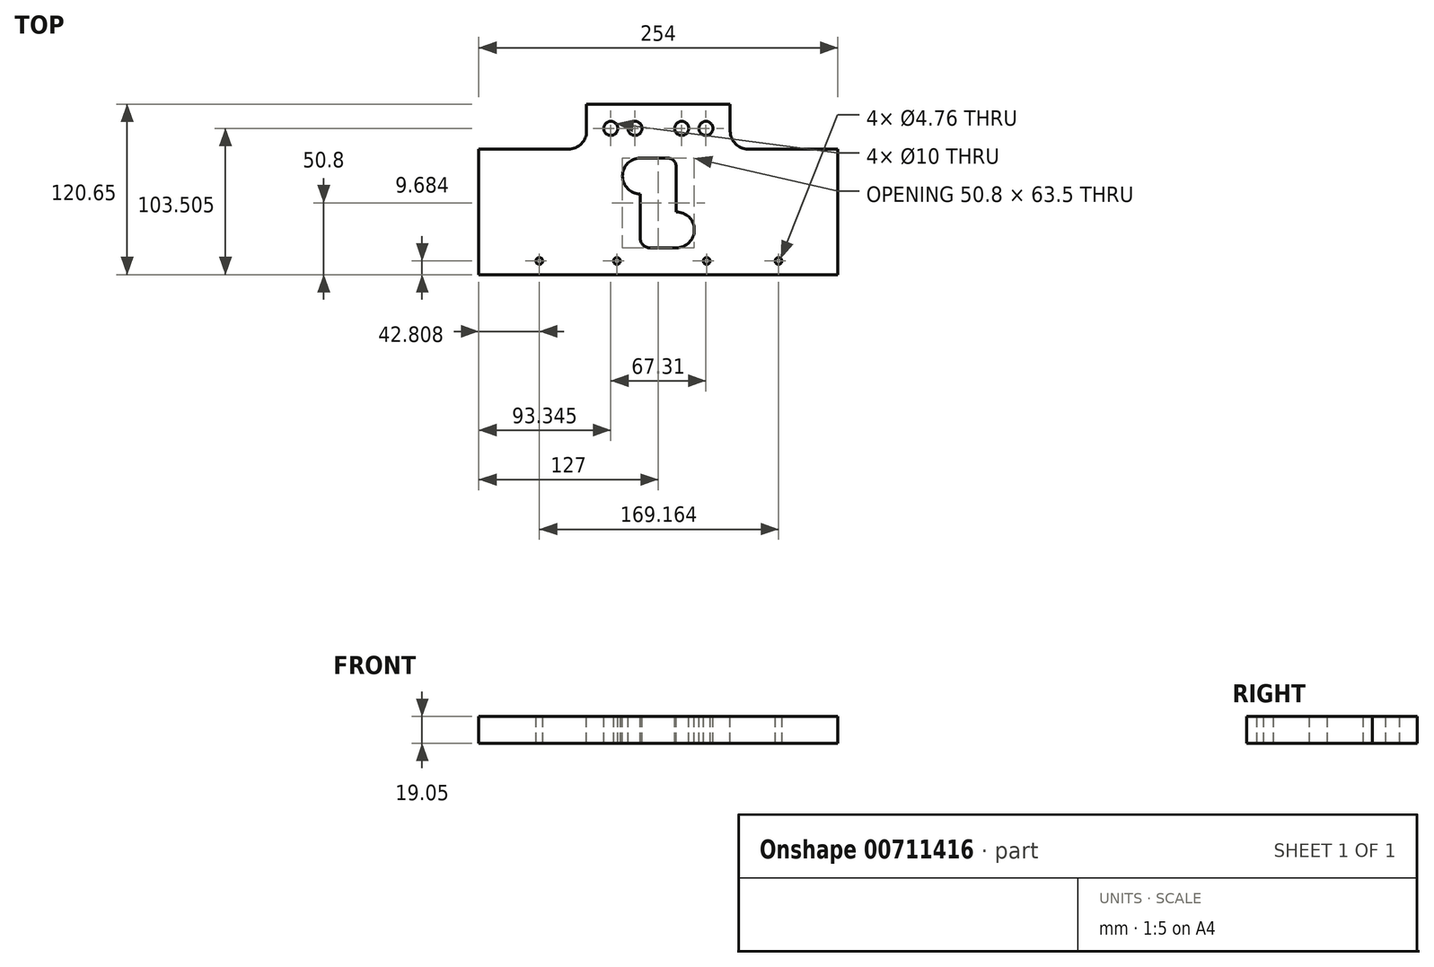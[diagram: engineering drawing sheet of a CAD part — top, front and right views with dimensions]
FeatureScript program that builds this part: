
annotation { "Feature Type Name" : "Feature", "Feature Type Description" : "" }
export const myFeature = defineFeature(function(context is Context, id is Id, definition is map)
    precondition{}
    {
        {
            var Q0;
            Q0=qCreatedBy(makeId("Top.planeOp"),FACE);
            var sketch = newSketch(context, id + "F0", { "sketchPlane" : qUnion([Q0])});
            skLineSegment(sketch, "E0.bottom", {"start": v(12.7, -31.75) * mm, "end": v(-6.35, -31.75) * mm});
            skLineSegment(sketch, "E0.top", {"start": v(6.35, 31.75) * mm, "end": v(-12.7, 31.75) * mm});
            skLineSegment(sketch, "E0.right", {"start": v(-12.7, -25.4) * mm, "end": v(-12.7, 6.35) * mm});
            skPoint(sketch, "E0.middle", {"position": v(0, 0) * mm});
            skArc(sketch, "E1", {"start": v(-12.7, 31.75) * mm, "mid": v(-25.4, 19.05) * mm, "end": v(-12.7, 6.35) * mm});
            skArc(sketch, "E2", {"start": v(12.7, -31.75) * mm, "mid": v(25.4, -19.05) * mm, "end": v(12.7, -6.35) * mm});
            skLineSegment(sketch, "E3.trimOffspring", {"start": v(12.7, -6.35) * mm, "end": v(12.7, 25.4) * mm});
            skPoint(sketch, "E4.visualSharp", {"position": v(-12.7, -31.75) * mm});
            skArc(sketch, "E4.filletArc", {"start": v(-12.7, -25.4) * mm, "mid": v(-10.84, -29.9) * mm, "end": v(-6.35, -31.75) * mm});
            skPoint(sketch, "E5.visualSharp", {"position": v(12.7, 31.75) * mm});
            skArc(sketch, "E5.filletArc", {"start": v(12.7, 25.4) * mm, "mid": v(10.84, 29.9) * mm, "end": v(6.35, 31.75) * mm});
            skLineSegment(sketch, "E6.bottom", {"start": v(0, -19.05) * mm, "end": v(-6.35, -19.05) * mm});
            skLineSegment(sketch, "E6.top", {"start": v(0, 19.05) * mm, "end": v(-6.35, 19.05) * mm});
            skLineSegment(sketch, "E6.left", {"start": v(6.35, -12.7) * mm, "end": v(6.35, 12.7) * mm});
            skLineSegment(sketch, "E6.right", {"start": v(-6.35, -19.05) * mm, "end": v(-6.35, 19.05) * mm});
            skPoint(sketch, "E7.visualSharp", {"position": v(6.35, 19.05) * mm});
            skArc(sketch, "E7.filletArc", {"start": v(6.35, 12.7) * mm, "mid": v(4.5, 17.2) * mm, "end": v(0, 19.05) * mm});
            skPoint(sketch, "E8.visualSharp", {"position": v(6.35, -19.05) * mm});
            skArc(sketch, "E8.filletArc", {"start": v(0, -19.05) * mm, "mid": v(4.5, -17.2) * mm, "end": v(6.35, -12.7) * mm});
            skLineSegment(sketch, "E9.top", {"start": v(50.8, -50.8) * mm, "end": v(-50.8, -50.8) * mm});
            skLineSegment(sketch, "E10.top", {"start": v(-50.8, 69.85) * mm, "end": v(50.8, 69.85) * mm});
            skLineSegment(sketch, "E11", {"start": v(50.8, -50.8) * mm, "end": v(50.8, -50.8) * mm});
            skLineSegment(sketch, "E12", {"start": v(-50.8, -50.8) * mm, "end": v(-50.8, -50.8) * mm});
            skCircle(sketch, "E13", {"center": v(-33.66, 52.7) * mm, "radius": 5 * mm});
            skCircle(sketch, "E14", {"center": v(-16.51, 52.7) * mm, "radius": 5 * mm});
            skCircle(sketch, "E15", {"center": v(16.5, 52.7) * mm, "radius": 5 * mm});
            skCircle(sketch, "E16", {"center": v(33.65, 52.7) * mm, "radius": 5 * mm});
            skLineSegment(sketch, "E17.top", {"start": v(127, 38.1) * mm, "end": v(63.5, 38.1) * mm});
            skLineSegment(sketch, "E17.left", {"start": v(127, -38.1) * mm, "end": v(127, 38.1) * mm});
            skLineSegment(sketch, "E17.right", {"start": v(-127, -38.1) * mm, "end": v(-127, 38.1) * mm});
            skLineSegment(sketch, "E18.trimOffspring", {"start": v(-63.5, 38.1) * mm, "end": v(-127, 38.1) * mm});
            skLineSegment(sketch, "E19", {"start": v(-50.8, 69.85) * mm, "end": v(-50.8, 50.8) * mm});
            skLineSegment(sketch, "E20", {"start": v(50.8, 69.85) * mm, "end": v(50.8, 50.8) * mm});
            skPoint(sketch, "E21.visualSharp", {"position": v(-50.8, 38.1) * mm});
            skArc(sketch, "E21.filletArc", {"start": v(-63.5, 38.1) * mm, "mid": v(-54.52, 41.82) * mm, "end": v(-50.8, 50.8) * mm});
            skPoint(sketch, "E22.visualSharp", {"position": v(50.8, 38.1) * mm});
            skArc(sketch, "E22.filletArc", {"start": v(50.8, 50.8) * mm, "mid": v(54.52, 41.82) * mm, "end": v(63.5, 38.1) * mm});
            skLineSegment(sketch, "E23.top", {"start": v(-127, -50.8) * mm, "end": v(-50.8, -50.8) * mm});
            skLineSegment(sketch, "E23.left", {"start": v(-127, -38.1) * mm, "end": v(-127, -50.8) * mm});
            skLineSegment(sketch, "E24.bottom", {"start": v(50.8, -50.8) * mm, "end": v(127, -50.8) * mm});
            skLineSegment(sketch, "E24.right", {"start": v(127, -50.8) * mm, "end": v(127, -38.1) * mm});
            skLineSegment(sketch, "E25", {"start": v(-45.75, 37.46) * mm, "end": v(40.3, 37.46) * mm, "construction": true});
            skLineSegment(sketch, "E26", {"start": v(-126.28, -38.74) * mm, "end": v(126.43, -38.74) * mm, "construction": true});
            skCircle(sketch, "E27", {"center": v(34.17, -41.12) * mm, "radius": 2.38 * mm});
            skLineSegment(sketch, "E28", {"start": v(34.17, -41.12) * mm, "end": v(124.12, -41.12) * mm});
            skLineSegment(sketch, "E29", {"start": v(34.17, -41.12) * mm, "end": v(-125.44, -41.12) * mm});
            skCircle(sketch, "E30", {"center": v(-29.33, -41.12) * mm, "radius": 2.38 * mm});
            skCircle(sketch, "E31.1.0.0", {"center": v(-84.2, -41.12) * mm, "radius": 2.38 * mm});
            skCircle(sketch, "E32.2.0.0", {"center": v(84.97, -41.12) * mm, "radius": 2.38 * mm});
            skLineSegment(sketch, "E32.direction1", {"start": v(34.17, -41.12) * mm, "end": v(59.57, -41.12) * mm, "construction": true});
            skSolve(sketch);
        }
        {
            var Q0;
            Q0 = qSketchRegion(id + "F0", true);
            extrude(context, id + "F1", {"entities" : qUnion([Q0]), "depth" : -19.05 * mm, "offsetDistance" : 25.4 * mm});
        }
        {
            var Q0;
            Q0=makeQuery(id+"F1.opExtrude","SWEPT_BODY",BODY,{"disambiguationData":[OSD([sQuery(id+"F0.wireOp",EDGE,"E0.bottom"),sQuery(id+"F0.wireOp",EDGE,"E0.top"),sQuery(id+"F0.wireOp",EDGE,"E0.right"),sQuery(id+"F0.wireOp",EDGE,"E1"),sQuery(id+"F0.wireOp",EDGE,"E2"),sQuery(id+"F0.wireOp",EDGE,"E3.trimOffspring"),sQuery(id+"F0.wireOp",EDGE,"E4.filletArc"),sQuery(id+"F0.wireOp",EDGE,"E5.filletArc"),sQuery(id+"F0.wireOp",EDGE,"E9.top"),sQuery(id+"F0.wireOp",EDGE,"E10.top"),sQuery(id+"F0.wireOp",EDGE,"E13"),sQuery(id+"F0.wireOp",EDGE,"E14"),sQuery(id+"F0.wireOp",EDGE,"E15"),sQuery(id+"F0.wireOp",EDGE,"E16"),sQuery(id+"F0.wireOp",EDGE,"E17.top"),sQuery(id+"F0.wireOp",EDGE,"E17.left"),sQuery(id+"F0.wireOp",EDGE,"E17.right"),sQuery(id+"F0.wireOp",EDGE,"E18.trimOffspring"),sQuery(id+"F0.wireOp",EDGE,"E19"),sQuery(id+"F0.wireOp",EDGE,"E20"),sQuery(id+"F0.wireOp",EDGE,"E21.filletArc"),sQuery(id+"F0.wireOp",EDGE,"E22.filletArc"),sQuery(id+"F0.wireOp",EDGE,"E23.top"),sQuery(id+"F0.wireOp",EDGE,"E23.left"),sQuery(id+"F0.wireOp",EDGE,"E24.bottom"),sQuery(id+"F0.wireOp",EDGE,"E24.right"),sQuery(id+"F0.wireOp",EDGE,"E27"),sQuery(id+"F0.wireOp",EDGE,"E30"),sQuery(id+"F0.wireOp",EDGE,"E31.1.0.0"),sQuery(id+"F0.wireOp",EDGE,"E32.2.0.0")])]});
            transform(context, id + "F2", {"entities" : qUnion([Q0]), "transformType" : TransformType.TRANSLATION_3D, "dx" : 0 * mm, "dy" : 0 * mm, "dz" : 0 * mm, "makeCopy" : true});
        }
        {
            var Q0;
            Q0=makeQuery(id+"F2.opPattern","COPY",BODY,{"derivedFrom":makeQuery(id+"F1.opExtrude","SWEPT_BODY",BODY,{"disambiguationData":[OSD([sQuery(id+"F0.wireOp",EDGE,"E0.bottom"),sQuery(id+"F0.wireOp",EDGE,"E0.top"),sQuery(id+"F0.wireOp",EDGE,"E0.right"),sQuery(id+"F0.wireOp",EDGE,"E1"),sQuery(id+"F0.wireOp",EDGE,"E2"),sQuery(id+"F0.wireOp",EDGE,"E3.trimOffspring"),sQuery(id+"F0.wireOp",EDGE,"E4.filletArc"),sQuery(id+"F0.wireOp",EDGE,"E5.filletArc"),sQuery(id+"F0.wireOp",EDGE,"E9.top"),sQuery(id+"F0.wireOp",EDGE,"E10.top"),sQuery(id+"F0.wireOp",EDGE,"E13"),sQuery(id+"F0.wireOp",EDGE,"E14"),sQuery(id+"F0.wireOp",EDGE,"E15"),sQuery(id+"F0.wireOp",EDGE,"E16"),sQuery(id+"F0.wireOp",EDGE,"E17.top"),sQuery(id+"F0.wireOp",EDGE,"E17.left"),sQuery(id+"F0.wireOp",EDGE,"E17.right"),sQuery(id+"F0.wireOp",EDGE,"E18.trimOffspring"),sQuery(id+"F0.wireOp",EDGE,"E19"),sQuery(id+"F0.wireOp",EDGE,"E20"),sQuery(id+"F0.wireOp",EDGE,"E21.filletArc"),sQuery(id+"F0.wireOp",EDGE,"E22.filletArc"),sQuery(id+"F0.wireOp",EDGE,"E23.top"),sQuery(id+"F0.wireOp",EDGE,"E23.left"),sQuery(id+"F0.wireOp",EDGE,"E24.bottom"),sQuery(id+"F0.wireOp",EDGE,"E24.right"),sQuery(id+"F0.wireOp",EDGE,"E27"),sQuery(id+"F0.wireOp",EDGE,"E30"),sQuery(id+"F0.wireOp",EDGE,"E31.1.0.0"),sQuery(id+"F0.wireOp",EDGE,"E32.2.0.0")])]}),"instanceName":"1"});
            deleteBodies(context, id + "F3", {"entities" : qUnion([Q0])});
        }
        {
            var Q0;
            Q0=makeQuery(id+"F1.opExtrude","SWEPT_BODY",BODY,{"disambiguationData":[OSD([sQuery(id+"F0.wireOp",EDGE,"E0.bottom"),sQuery(id+"F0.wireOp",EDGE,"E0.top"),sQuery(id+"F0.wireOp",EDGE,"E0.right"),sQuery(id+"F0.wireOp",EDGE,"E1"),sQuery(id+"F0.wireOp",EDGE,"E2"),sQuery(id+"F0.wireOp",EDGE,"E3.trimOffspring"),sQuery(id+"F0.wireOp",EDGE,"E4.filletArc"),sQuery(id+"F0.wireOp",EDGE,"E5.filletArc"),sQuery(id+"F0.wireOp",EDGE,"E9.top"),sQuery(id+"F0.wireOp",EDGE,"E10.top"),sQuery(id+"F0.wireOp",EDGE,"E13"),sQuery(id+"F0.wireOp",EDGE,"E14"),sQuery(id+"F0.wireOp",EDGE,"E15"),sQuery(id+"F0.wireOp",EDGE,"E16"),sQuery(id+"F0.wireOp",EDGE,"E17.top"),sQuery(id+"F0.wireOp",EDGE,"E17.left"),sQuery(id+"F0.wireOp",EDGE,"E17.right"),sQuery(id+"F0.wireOp",EDGE,"E18.trimOffspring"),sQuery(id+"F0.wireOp",EDGE,"E19"),sQuery(id+"F0.wireOp",EDGE,"E20"),sQuery(id+"F0.wireOp",EDGE,"E21.filletArc"),sQuery(id+"F0.wireOp",EDGE,"E22.filletArc"),sQuery(id+"F0.wireOp",EDGE,"E23.top"),sQuery(id+"F0.wireOp",EDGE,"E23.left"),sQuery(id+"F0.wireOp",EDGE,"E24.bottom"),sQuery(id+"F0.wireOp",EDGE,"E24.right"),sQuery(id+"F0.wireOp",EDGE,"E27"),sQuery(id+"F0.wireOp",EDGE,"E30"),sQuery(id+"F0.wireOp",EDGE,"E31.1.0.0"),sQuery(id+"F0.wireOp",EDGE,"E32.2.0.0")])]});
            transform(context, id + "F4", {"entities" : qUnion([Q0]), "transformType" : TransformType.TRANSLATION_3D, "dx" : 0 * mm, "dy" : 0 * mm, "dz" : 0 * mm, "makeCopy" : true});
        }
        {
            var Q0;
            Q0=makeQuery(id+"F4.opPattern","COPY",BODY,{"derivedFrom":makeQuery(id+"F1.opExtrude","SWEPT_BODY",BODY,{"disambiguationData":[OSD([sQuery(id+"F0.wireOp",EDGE,"E0.bottom"),sQuery(id+"F0.wireOp",EDGE,"E0.top"),sQuery(id+"F0.wireOp",EDGE,"E0.right"),sQuery(id+"F0.wireOp",EDGE,"E1"),sQuery(id+"F0.wireOp",EDGE,"E2"),sQuery(id+"F0.wireOp",EDGE,"E3.trimOffspring"),sQuery(id+"F0.wireOp",EDGE,"E4.filletArc"),sQuery(id+"F0.wireOp",EDGE,"E5.filletArc"),sQuery(id+"F0.wireOp",EDGE,"E9.top"),sQuery(id+"F0.wireOp",EDGE,"E10.top"),sQuery(id+"F0.wireOp",EDGE,"E13"),sQuery(id+"F0.wireOp",EDGE,"E14"),sQuery(id+"F0.wireOp",EDGE,"E15"),sQuery(id+"F0.wireOp",EDGE,"E16"),sQuery(id+"F0.wireOp",EDGE,"E17.top"),sQuery(id+"F0.wireOp",EDGE,"E17.left"),sQuery(id+"F0.wireOp",EDGE,"E17.right"),sQuery(id+"F0.wireOp",EDGE,"E18.trimOffspring"),sQuery(id+"F0.wireOp",EDGE,"E19"),sQuery(id+"F0.wireOp",EDGE,"E20"),sQuery(id+"F0.wireOp",EDGE,"E21.filletArc"),sQuery(id+"F0.wireOp",EDGE,"E22.filletArc"),sQuery(id+"F0.wireOp",EDGE,"E23.top"),sQuery(id+"F0.wireOp",EDGE,"E23.left"),sQuery(id+"F0.wireOp",EDGE,"E24.bottom"),sQuery(id+"F0.wireOp",EDGE,"E24.right"),sQuery(id+"F0.wireOp",EDGE,"E27"),sQuery(id+"F0.wireOp",EDGE,"E30"),sQuery(id+"F0.wireOp",EDGE,"E31.1.0.0"),sQuery(id+"F0.wireOp",EDGE,"E32.2.0.0")])]}),"instanceName":"1"});
            deleteBodies(context, id + "F5", {"entities" : qUnion([Q0])});
        }
    });
